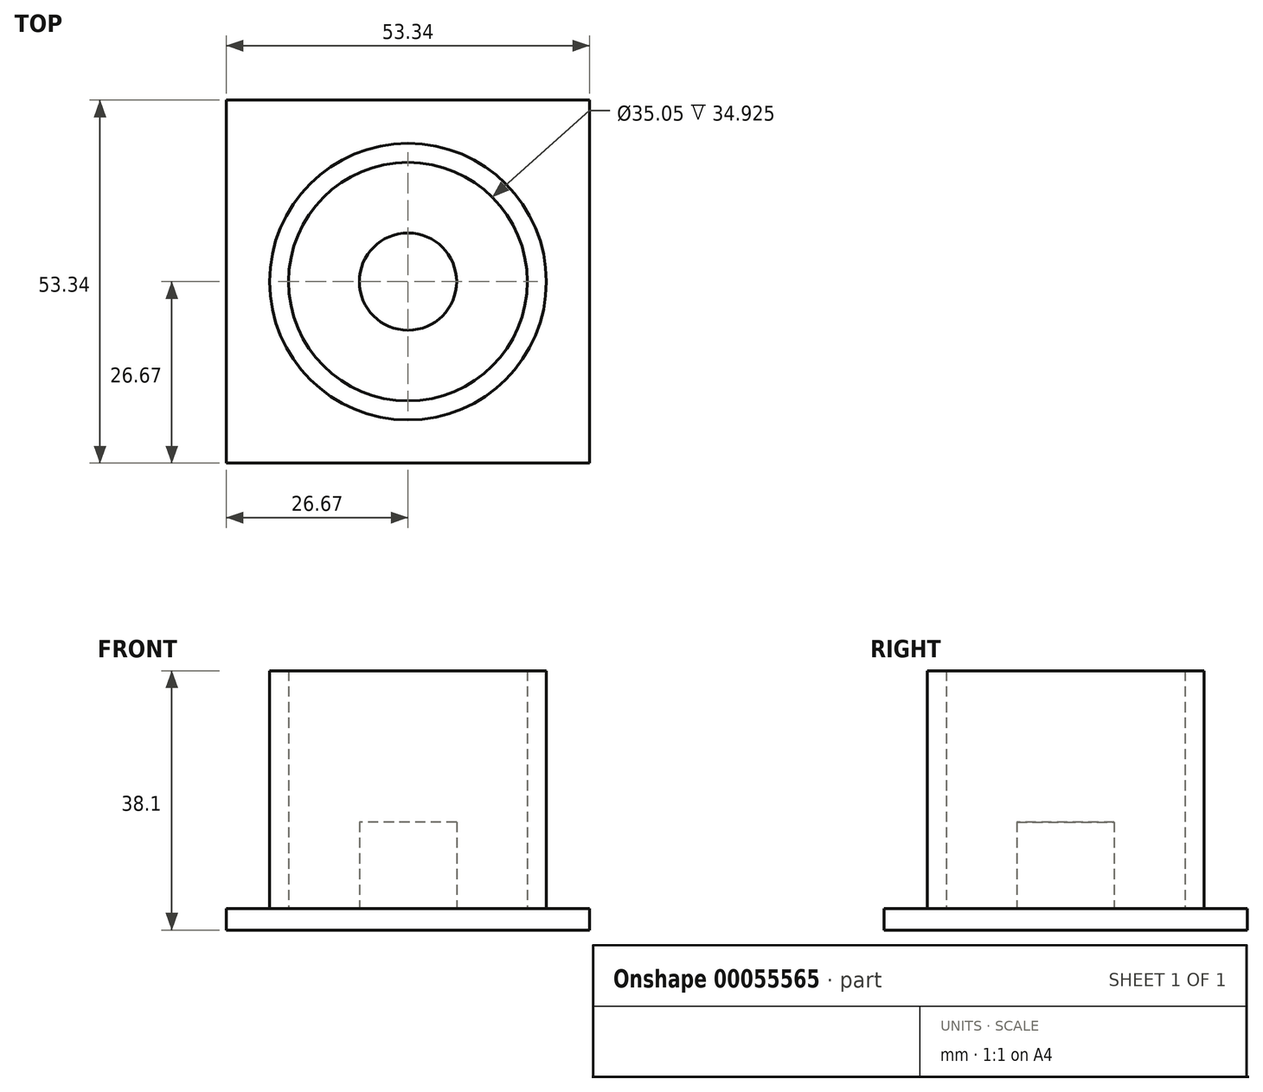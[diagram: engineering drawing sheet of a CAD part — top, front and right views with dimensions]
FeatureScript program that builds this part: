
annotation { "Feature Type Name" : "Feature", "Feature Type Description" : "" }
export const myFeature = defineFeature(function(context is Context, id is Id, definition is map)
    precondition{}
    {
        {
            var Q0;
            Q0=qCreatedBy(makeId("Top.planeOp"),FACE);
            var sketch = newSketch(context, id + "F0", { "sketchPlane" : qUnion([Q0])});
            skCircle(sketch, "E0", {"center": v(0, 0) * mm, "radius": 17.53 * mm});
            skCircle(sketch, "E1", {"center": v(0, 0) * mm, "radius": 20.32 * mm});
            skSolve(sketch);
        }
        {
            var Q0;
            Q0=makeQuery(id+"F0.imprint","IMPRINT",FACE,{"disambiguationData":[TD([[makeQuery(id+"F0.imprint","IMPRINT",EDGE,{"derivedFrom":sQuery(id+"F0.wireOp",EDGE,"E0")}),-1.0]])]});
            extrude(context, id + "F1", {"entities" : qUnion([Q0]), "depth" : 38.1 * mm});
        }
        {
            var Q0;
            Q0=qCreatedBy(makeId("Top.planeOp"),FACE);
            var sketch = newSketch(context, id + "F2", { "sketchPlane" : qUnion([Q0])});
            skLineSegment(sketch, "E2.bottom", {"start": v(-26.67, -26.67) * mm, "end": v(26.67, -26.67) * mm});
            skLineSegment(sketch, "E2.top", {"start": v(-26.67, 26.67) * mm, "end": v(26.67, 26.67) * mm});
            skLineSegment(sketch, "E2.left", {"start": v(-26.67, -26.67) * mm, "end": v(-26.67, 26.67) * mm});
            skLineSegment(sketch, "E2.right", {"start": v(26.67, -26.67) * mm, "end": v(26.67, 26.67) * mm});
            skSolve(sketch);
        }
        {
            var Q0;
            Q0=makeQuery(id+"F2.imprint","IMPRINT",FACE,{"disambiguationData":[TD([[makeQuery(id+"F2.imprint","IMPRINT",EDGE,{"derivedFrom":sQuery(id+"F2.wireOp",EDGE,"E2.bottom")}),1.0]])]});
            extrude(context, id + "F3", {"entities" : qUnion([Q0]), "operationType" : NewBodyOperationType.ADD, "depth" : 3.17 * mm});
        }
        {
            var Q0;
            Q0=makeQuery(id+"F3.boolean.opBoolean","SPLIT",FACE,{"disambiguationData":[TD([makeQuery(id+"F1.opExtrude","SWEPT_FACE",FACE,{"disambiguationData":[OSD([sQuery(id+"F0.wireOp",EDGE,"E0")])]})])],"derivedFrom":makeQuery(id+"F3.opExtrude","CAP_FACE",FACE,{"disambiguationData":[OSD([sQuery(id+"F2.wireOp",EDGE,"E2.bottom"),sQuery(id+"F2.wireOp",EDGE,"E2.top"),sQuery(id+"F2.wireOp",EDGE,"E2.left"),sQuery(id+"F2.wireOp",EDGE,"E2.right")])],"isStart":false})});
            var sketch = newSketch(context, id + "F4", { "sketchPlane" : qUnion([Q0])});
            skCircle(sketch, "E3", {"center": v(0, 0) * mm, "radius": 7.14 * mm});
            skSolve(sketch);
        }
        {
            var Q0;
            Q0=makeQuery(id+"F4.imprint","IMPRINT",FACE,{"disambiguationData":[TD([[makeQuery(id+"F4.imprint","IMPRINT",EDGE,{"derivedFrom":sQuery(id+"F4.wireOp",EDGE,"E3")}),1.0]])]});
            extrude(context, id + "F5", {"entities" : qUnion([Q0]), "operationType" : NewBodyOperationType.ADD, "depth" : 12.7 * mm});
        }
    });
